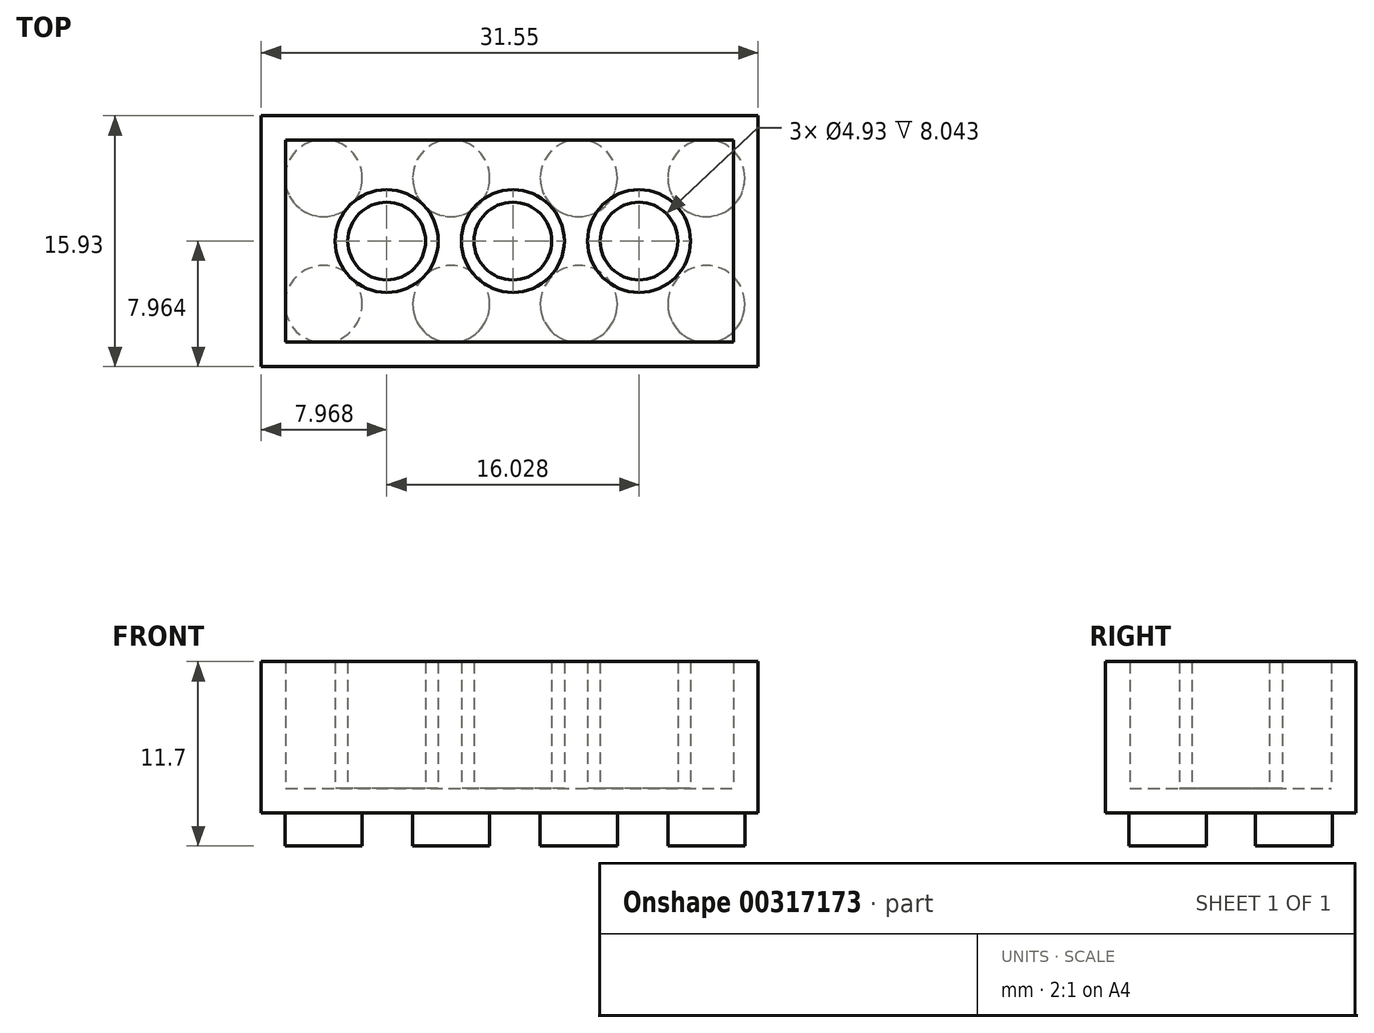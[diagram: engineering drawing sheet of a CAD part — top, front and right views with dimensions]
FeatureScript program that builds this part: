
annotation { "Feature Type Name" : "Feature", "Feature Type Description" : "" }
export const myFeature = defineFeature(function(context is Context, id is Id, definition is map)
    precondition{}
    {
        {
            var Q0;
            Q0=qCreatedBy(makeId("Top.planeOp"),FACE);
            var sketch = newSketch(context, id + "F0", { "sketchPlane" : qUnion([Q0])});
            skLineSegment(sketch, "E0.bottom", {"start": v(-36.9, -20.53) * mm, "end": v(-5.36, -20.53) * mm});
            skLineSegment(sketch, "E0.top", {"start": v(-36.9, -4.6) * mm, "end": v(-5.36, -4.6) * mm});
            skLineSegment(sketch, "E0.left", {"start": v(-36.9, -20.53) * mm, "end": v(-36.9, -4.6) * mm});
            skLineSegment(sketch, "E0.right", {"start": v(-5.36, -20.53) * mm, "end": v(-5.36, -4.6) * mm});
            skLineSegment(sketch, "E1.bottom", {"start": v(-35.35, -18.97) * mm, "end": v(-6.91, -18.97) * mm});
            skLineSegment(sketch, "E1.top", {"start": v(-35.35, -6.16) * mm, "end": v(-6.91, -6.16) * mm});
            skLineSegment(sketch, "E1.left", {"start": v(-35.35, -18.97) * mm, "end": v(-35.35, -6.16) * mm});
            skLineSegment(sketch, "E1.right", {"start": v(-6.91, -18.97) * mm, "end": v(-6.91, -6.16) * mm});
            skSolve(sketch);
        }
        {
            var Q0;
            Q0 = qSketchRegion(id + "F0", true);
            var Q1;
            Q1=makeQuery(id+"F0.imprint","IMPRINT",FACE,{"disambiguationData":[TD([[makeQuery(id+"F0.imprint","IMPRINT",EDGE,{"derivedFrom":sQuery(id+"F0.wireOp",EDGE,"E1.bottom")}),1.0]])]});
            extrude(context, id + "F1", {"entities" : qUnion([Q0, Q1]), "depth" : 9.6 * mm});
        }
        {
            var Q0;
            Q0=makeQuery(id+"F0.imprint","IMPRINT",FACE,{"disambiguationData":[TD([[makeQuery(id+"F0.imprint","IMPRINT",EDGE,{"derivedFrom":sQuery(id+"F0.wireOp",EDGE,"E1.bottom")}),1.0]])]});
            extrude(context, id + "F2", {"entities" : qUnion([Q0]), "operationType" : NewBodyOperationType.REMOVE, "depth" : 25 * mm});
        }
        {
            var Q0;
            Q0=makeQuery(id+"F0.imprint","IMPRINT",FACE,{"disambiguationData":[TD([[makeQuery(id+"F0.imprint","IMPRINT",EDGE,{"derivedFrom":sQuery(id+"F0.wireOp",EDGE,"E1.bottom")}),1.0]])]});
            extrude(context, id + "F3", {"entities" : qUnion([Q0]), "operationType" : NewBodyOperationType.ADD, "depth" : 1.56 * mm});
        }
        {
            var Q0;
            Q0=makeQuery(id+"F3.opExtrude","CAP_FACE",FACE,{"disambiguationData":[OSD([sQuery(id+"F0.wireOp",EDGE,"E1.bottom"),sQuery(id+"F0.wireOp",EDGE,"E1.top"),sQuery(id+"F0.wireOp",EDGE,"E1.left"),sQuery(id+"F0.wireOp",EDGE,"E1.right")])],"isStart":false});
            var sketch = newSketch(context, id + "F4", { "sketchPlane" : qUnion([Q0])});
            skCircle(sketch, "E2", {"center": v(-28.94, -12.57) * mm, "radius": 2.47 * mm});
            skCircle(sketch, "E3", {"center": v(-28.94, -12.57) * mm, "radius": 3.27 * mm});
            skCircle(sketch, "E4", {"center": v(-20.93, -12.57) * mm, "radius": 2.47 * mm});
            skCircle(sketch, "E5", {"center": v(-20.93, -12.57) * mm, "radius": 3.27 * mm});
            skCircle(sketch, "E6", {"center": v(-12.91, -12.57) * mm, "radius": 2.47 * mm});
            skCircle(sketch, "E7", {"center": v(-12.91, -12.57) * mm, "radius": 3.27 * mm});
            skSolve(sketch);
        }
        {
            var Q0;
            Q0=makeQuery(id+"F4.imprint","IMPRINT",FACE,{"disambiguationData":[TD([[makeQuery(id+"F4.imprint","IMPRINT",EDGE,{"derivedFrom":sQuery(id+"F4.wireOp",EDGE,"E2")}),-1.0]])]});
            var Q1;
            Q1=makeQuery(id+"F4.imprint","IMPRINT",FACE,{"disambiguationData":[TD([[makeQuery(id+"F4.imprint","IMPRINT",EDGE,{"derivedFrom":sQuery(id+"F4.wireOp",EDGE,"E4")}),-1.0]])]});
            var Q2;
            Q2=makeQuery(id+"F4.imprint","IMPRINT",FACE,{"disambiguationData":[TD([[makeQuery(id+"F4.imprint","IMPRINT",EDGE,{"derivedFrom":sQuery(id+"F4.wireOp",EDGE,"E6")}),-1.0]])]});
            extrude(context, id + "F5", {"entities" : qUnion([Q0, Q1, Q2]), "operationType" : NewBodyOperationType.ADD, "depth" : 8.04 * mm});
        }
        {
            var Q0;
            Q0=makeQuery(id+"F3.boolean.opBoolean","MERGE",FACE,{"derivedFrom":[makeQuery(id+"F1.opExtrude","CAP_FACE",FACE,{"disambiguationData":[OSD([sQuery(id+"F0.wireOp",EDGE,"E0.bottom"),sQuery(id+"F0.wireOp",EDGE,"E0.top"),sQuery(id+"F0.wireOp",EDGE,"E0.left"),sQuery(id+"F0.wireOp",EDGE,"E0.right")])],"isStart":true}),makeQuery(id+"F3.opExtrude","CAP_FACE",FACE,{"disambiguationData":[OSD([sQuery(id+"F0.wireOp",EDGE,"E1.bottom"),sQuery(id+"F0.wireOp",EDGE,"E1.top"),sQuery(id+"F0.wireOp",EDGE,"E1.left"),sQuery(id+"F0.wireOp",EDGE,"E1.right")])],"isStart":true})]});
            var sketch = newSketch(context, id + "F6", { "sketchPlane" : qUnion([Q0])});
            skCircle(sketch, "E8", {"center": v(-32.95, 16.57) * mm, "radius": 2.45 * mm});
            skCircle(sketch, "E9", {"center": v(-24.84, 16.57) * mm, "radius": 2.45 * mm});
            skCircle(sketch, "E10", {"center": v(-16.74, 16.57) * mm, "radius": 2.45 * mm});
            skCircle(sketch, "E11", {"center": v(-8.64, 16.57) * mm, "radius": 2.45 * mm});
            skCircle(sketch, "E12", {"center": v(-32.95, 8.56) * mm, "radius": 2.45 * mm});
            skCircle(sketch, "E13", {"center": v(-24.84, 8.56) * mm, "radius": 2.45 * mm});
            skCircle(sketch, "E14", {"center": v(-16.74, 8.56) * mm, "radius": 2.45 * mm});
            skCircle(sketch, "E15", {"center": v(-8.64, 8.56) * mm, "radius": 2.45 * mm});
            skSolve(sketch);
        }
        {
            var Q0;
            Q0=makeQuery(id+"F6.imprint","IMPRINT",FACE,{"disambiguationData":[TD([[makeQuery(id+"F6.imprint","IMPRINT",EDGE,{"derivedFrom":sQuery(id+"F6.wireOp",EDGE,"E8")}),1.0]])]});
            var Q1;
            Q1=makeQuery(id+"F6.imprint","IMPRINT",FACE,{"disambiguationData":[TD([[makeQuery(id+"F6.imprint","IMPRINT",EDGE,{"derivedFrom":sQuery(id+"F6.wireOp",EDGE,"E9")}),1.0]])]});
            var Q2;
            Q2=makeQuery(id+"F6.imprint","IMPRINT",FACE,{"disambiguationData":[TD([[makeQuery(id+"F6.imprint","IMPRINT",EDGE,{"derivedFrom":sQuery(id+"F6.wireOp",EDGE,"E10")}),1.0]])]});
            var Q3;
            Q3=makeQuery(id+"F6.imprint","IMPRINT",FACE,{"disambiguationData":[TD([[makeQuery(id+"F6.imprint","IMPRINT",EDGE,{"derivedFrom":sQuery(id+"F6.wireOp",EDGE,"E11")}),1.0]])]});
            var Q4;
            Q4=makeQuery(id+"F6.imprint","IMPRINT",FACE,{"disambiguationData":[TD([[makeQuery(id+"F6.imprint","IMPRINT",EDGE,{"derivedFrom":sQuery(id+"F6.wireOp",EDGE,"E15")}),1.0]])]});
            var Q5;
            Q5=makeQuery(id+"F6.imprint","IMPRINT",FACE,{"disambiguationData":[TD([[makeQuery(id+"F6.imprint","IMPRINT",EDGE,{"derivedFrom":sQuery(id+"F6.wireOp",EDGE,"E14")}),1.0]])]});
            var Q6;
            Q6=makeQuery(id+"F6.imprint","IMPRINT",FACE,{"disambiguationData":[TD([[makeQuery(id+"F6.imprint","IMPRINT",EDGE,{"derivedFrom":sQuery(id+"F6.wireOp",EDGE,"E13")}),1.0]])]});
            var Q7;
            Q7=makeQuery(id+"F6.imprint","IMPRINT",FACE,{"disambiguationData":[TD([[makeQuery(id+"F6.imprint","IMPRINT",EDGE,{"derivedFrom":sQuery(id+"F6.wireOp",EDGE,"E12")}),1.0]])]});
            extrude(context, id + "F7", {"entities" : qUnion([Q0, Q1, Q2, Q3, Q4, Q5, Q6, Q7]), "operationType" : NewBodyOperationType.ADD, "depth" : 2.1 * mm});
        }
    });
